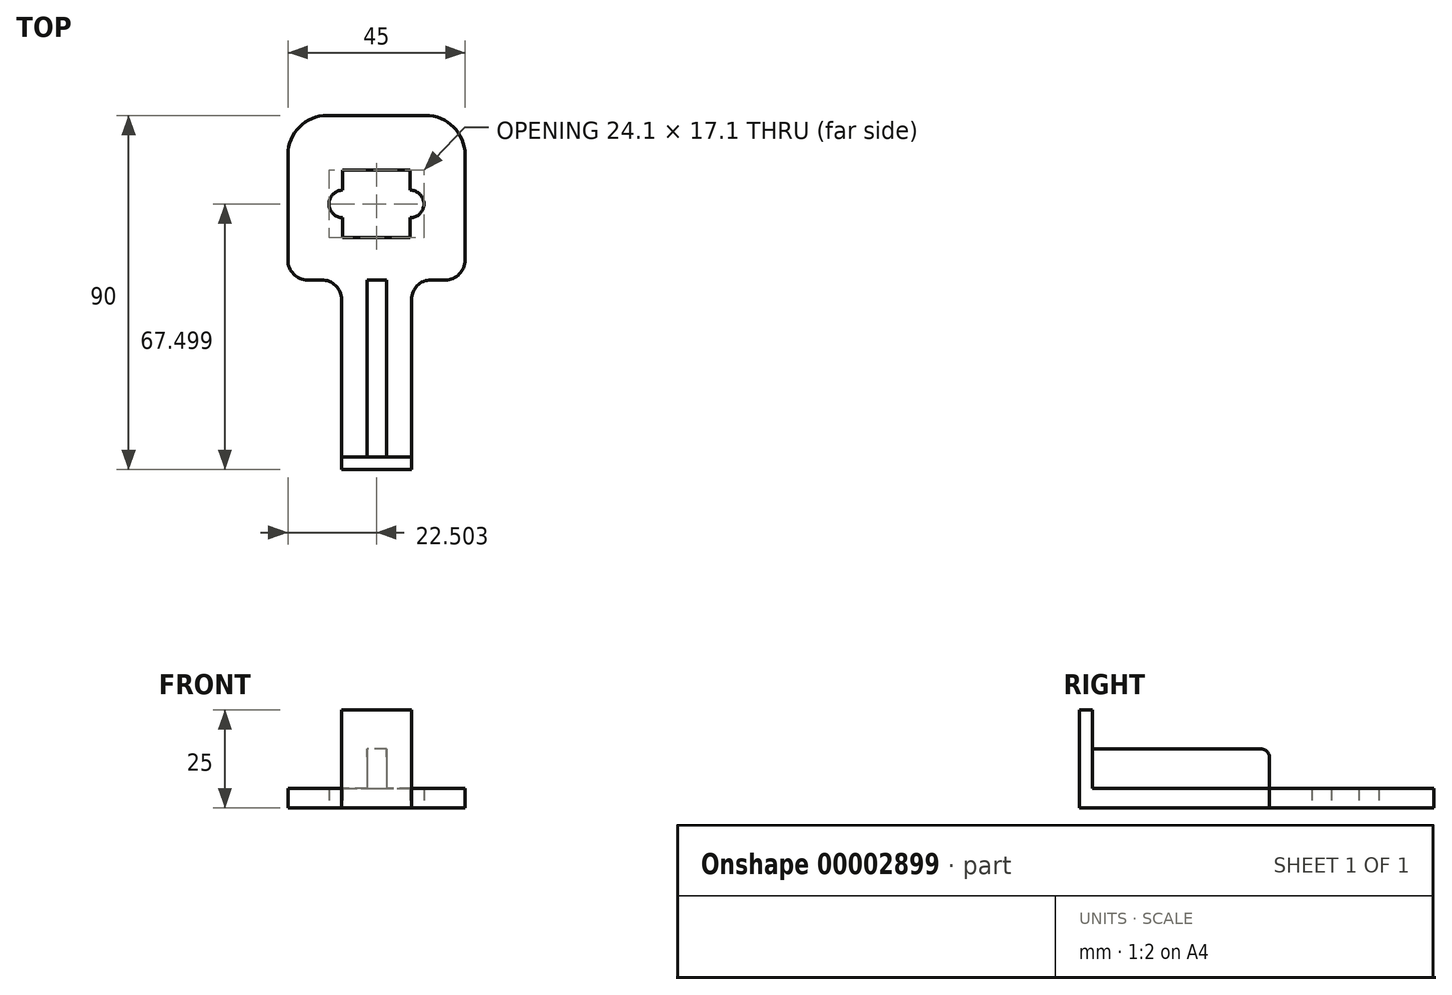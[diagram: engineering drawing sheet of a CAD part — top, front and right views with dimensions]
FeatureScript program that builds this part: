
annotation { "Feature Type Name" : "Feature", "Feature Type Description" : "" }
export const myFeature = defineFeature(function(context is Context, id is Id, definition is map)
    precondition{}
    {
        {
            var Q0;
            Q0=qCreatedBy(makeId("Top.planeOp"),FACE);
            var sketch = newSketch(context, id + "F0", { "sketchPlane" : qUnion([Q0])});
            skLineSegment(sketch, "E0.bottom", {"start": v(-64.63, 13.52) * mm, "end": v(-47.53, 13.52) * mm});
            skLineSegment(sketch, "E0.top", {"start": v(-64.63, -3.58) * mm, "end": v(-47.53, -3.58) * mm});
            skLineSegment(sketch, "E0.left", {"start": v(-64.63, 13.52) * mm, "end": v(-64.63, 8.47) * mm});
            skLineSegment(sketch, "E0.right", {"start": v(-47.53, 13.52) * mm, "end": v(-47.53, 8.47) * mm});
            skArc(sketch, "E1", {"start": v(-64.63, 8.47) * mm, "mid": v(-68.13, 4.97) * mm, "end": v(-64.63, 1.47) * mm});
            skArc(sketch, "E2", {"start": v(-47.53, 1.47) * mm, "mid": v(-44.03, 4.97) * mm, "end": v(-47.53, 8.47) * mm});
            skLineSegment(sketch, "E3.trimOffspring", {"start": v(-64.63, 1.47) * mm, "end": v(-64.63, -3.58) * mm});
            skLineSegment(sketch, "E4.trimOffspring", {"start": v(-47.53, 1.47) * mm, "end": v(-47.53, -3.58) * mm});
            skLineSegment(sketch, "E5.bottom", {"start": v(-68.58, 27.47) * mm, "end": v(-43.58, 27.47) * mm});
            skLineSegment(sketch, "E5.top", {"start": v(-64.97, -62.53) * mm, "end": v(-47.18, -62.53) * mm});
            skLineSegment(sketch, "E5.left", {"start": v(-78.58, 17.47) * mm, "end": v(-78.58, -9.33) * mm});
            skLineSegment(sketch, "E5.right", {"start": v(-33.58, 17.47) * mm, "end": v(-33.58, -9.33) * mm});
            skPoint(sketch, "E6.visualSharp", {"position": v(-78.58, 27.47) * mm});
            skArc(sketch, "E6.filletArc", {"start": v(-68.58, 27.47) * mm, "mid": v(-75.65, 24.54) * mm, "end": v(-78.58, 17.47) * mm});
            skPoint(sketch, "E7.visualSharp", {"position": v(-33.58, 27.47) * mm});
            skArc(sketch, "E7.filletArc", {"start": v(-33.58, 17.47) * mm, "mid": v(-36.5, 24.54) * mm, "end": v(-43.58, 27.47) * mm});
            skLineSegment(sketch, "E8.bottom", {"start": v(-73.58, -14.33) * mm, "end": v(-69.97, -14.33) * mm});
            skLineSegment(sketch, "E8.right", {"start": v(-64.97, -19.33) * mm, "end": v(-64.97, -62.53) * mm});
            skLineSegment(sketch, "E9.0.MirrorCS", {"start": v(-38.58, -14.33) * mm, "end": v(-42.18, -14.33) * mm});
            skLineSegment(sketch, "E9.1.MirrorCS", {"start": v(-47.18, -19.33) * mm, "end": v(-47.18, -62.53) * mm});
            skPoint(sketch, "E10.orphan", {"position": v(-33.58, -62.53) * mm});
            skPoint(sketch, "E11.visualSharp", {"position": v(-78.58, -14.33) * mm});
            skArc(sketch, "E11.filletArc", {"start": v(-78.58, -9.33) * mm, "mid": v(-77.11, -12.86) * mm, "end": v(-73.58, -14.33) * mm});
            skPoint(sketch, "E12.visualSharp", {"position": v(-64.97, -14.33) * mm});
            skArc(sketch, "E12.filletArc", {"start": v(-64.97, -19.33) * mm, "mid": v(-66.43, -15.8) * mm, "end": v(-69.97, -14.33) * mm});
            skPoint(sketch, "E13.visualSharp", {"position": v(-47.18, -14.33) * mm});
            skArc(sketch, "E13.filletArc", {"start": v(-42.18, -14.33) * mm, "mid": v(-45.72, -15.8) * mm, "end": v(-47.18, -19.33) * mm});
            skPoint(sketch, "E14.visualSharp", {"position": v(-33.58, -14.33) * mm});
            skArc(sketch, "E14.filletArc", {"start": v(-38.58, -14.33) * mm, "mid": v(-35.04, -12.86) * mm, "end": v(-33.58, -9.33) * mm});
            skLineSegment(sketch, "E15", {"start": v(-64.97, -59.3) * mm, "end": v(-47.18, -59.3) * mm});
            skSolve(sketch);
        }
        {
            var Q0;
            Q0 = qSketchRegion(id + "F0", true);
            extrude(context, id + "F1", {"entities" : qUnion([Q0]), "depth" : 5 * mm});
        }
        {
            var Q0;
            {var subQ2=sQuery(id+"F0.wireOp",EDGE,"E5.top");Q0=makeQuery(id+"F0.imprint","IMPRINT",FACE,{"disambiguationData":[TD([[makeQuery(id+"F0.imprint","IMPRINT",EDGE,{"derivedFrom":subQ2}),1.0]])]});}
            extrude(context, id + "F2", {"entities" : qUnion([Q0]), "operationType" : NewBodyOperationType.ADD, "depth" : 25 * mm});
        }
        {
            var Q0;
            Q0=makeQuery(id+"F1.opExtrude","CAP_FACE",FACE,{"disambiguationData":[OSD([sQuery(id+"F0.wireOp",EDGE,"E0.bottom"),sQuery(id+"F0.wireOp",EDGE,"E0.top"),sQuery(id+"F0.wireOp",EDGE,"E0.left"),sQuery(id+"F0.wireOp",EDGE,"E0.right"),sQuery(id+"F0.wireOp",EDGE,"E1"),sQuery(id+"F0.wireOp",EDGE,"E2"),sQuery(id+"F0.wireOp",EDGE,"E3.trimOffspring"),sQuery(id+"F0.wireOp",EDGE,"E4.trimOffspring"),sQuery(id+"F0.wireOp",EDGE,"E5.bottom"),sQuery(id+"F0.wireOp",EDGE,"E5.top"),sQuery(id+"F0.wireOp",EDGE,"E5.left"),sQuery(id+"F0.wireOp",EDGE,"E5.right"),sQuery(id+"F0.wireOp",EDGE,"E6.filletArc"),sQuery(id+"F0.wireOp",EDGE,"E7.filletArc"),sQuery(id+"F0.wireOp",EDGE,"E8.bottom"),sQuery(id+"F0.wireOp",EDGE,"E8.right"),sQuery(id+"F0.wireOp",EDGE,"E9.0.MirrorCS"),sQuery(id+"F0.wireOp",EDGE,"E9.1.MirrorCS"),sQuery(id+"F0.wireOp",EDGE,"E11.filletArc"),sQuery(id+"F0.wireOp",EDGE,"E12.filletArc"),sQuery(id+"F0.wireOp",EDGE,"E13.filletArc"),sQuery(id+"F0.wireOp",EDGE,"E14.filletArc")])],"isStart":false});
            var sketch = newSketch(context, id + "F3", { "sketchPlane" : qUnion([Q0])});
            skLineSegment(sketch, "E16.bottom", {"start": v(-58.46, -14.33) * mm, "end": v(-53.5, -14.33) * mm});
            skLineSegment(sketch, "E16.top", {"start": v(-58.46, -59.3) * mm, "end": v(-53.5, -59.3) * mm});
            skLineSegment(sketch, "E16.left", {"start": v(-58.46, -14.33) * mm, "end": v(-58.46, -59.3) * mm});
            skLineSegment(sketch, "E16.right", {"start": v(-53.5, -14.33) * mm, "end": v(-53.5, -59.3) * mm});
            skSolve(sketch);
        }
        {
            var Q0;
            Q0=makeQuery(id+"F3.imprint","IMPRINT",FACE,{"disambiguationData":[TD([[makeQuery(id+"F3.imprint","IMPRINT",EDGE,{"derivedFrom":sQuery(id+"F3.wireOp",EDGE,"E16.bottom")}),-1.0]])]});
            extrude(context, id + "F4", {"entities" : qUnion([Q0]), "operationType" : NewBodyOperationType.ADD, "depth" : 10 * mm});
        }
        {
            var Q0;
            Q0=makeQuery(id+"F4.opExtrude","CAP_EDGE",EDGE,{"disambiguationData":[OSD([sQuery(id+"F3.wireOp",EDGE,"E16.right")])],"isStart":true});
            var Q1;
            Q1=makeQuery(id+"F4.opExtrude","SWEPT_EDGE",EDGE,{"disambiguationData":[OSD([sQuery(id+"F0.wireOp",EDGE,"E0.bottom"),sQuery(id+"F0.wireOp",EDGE,"E0.top"),sQuery(id+"F0.wireOp",EDGE,"E0.left"),sQuery(id+"F0.wireOp",EDGE,"E0.right"),sQuery(id+"F0.wireOp",EDGE,"E1"),sQuery(id+"F0.wireOp",EDGE,"E2"),sQuery(id+"F0.wireOp",EDGE,"E3.trimOffspring"),sQuery(id+"F0.wireOp",EDGE,"E4.trimOffspring"),sQuery(id+"F0.wireOp",EDGE,"E5.bottom"),sQuery(id+"F0.wireOp",EDGE,"E5.top"),sQuery(id+"F0.wireOp",EDGE,"E5.left"),sQuery(id+"F0.wireOp",EDGE,"E5.right"),sQuery(id+"F0.wireOp",EDGE,"E6.filletArc"),sQuery(id+"F0.wireOp",EDGE,"E7.filletArc"),sQuery(id+"F0.wireOp",EDGE,"E8.bottom"),sQuery(id+"F0.wireOp",EDGE,"E8.right"),sQuery(id+"F0.wireOp",EDGE,"E9.0.MirrorCS"),sQuery(id+"F0.wireOp",EDGE,"E9.1.MirrorCS"),sQuery(id+"F0.wireOp",EDGE,"E11.filletArc"),sQuery(id+"F0.wireOp",EDGE,"E12.filletArc"),sQuery(id+"F0.wireOp",EDGE,"E13.filletArc"),sQuery(id+"F0.wireOp",EDGE,"E14.filletArc"),sQuery(id+"F0.wireOp",EDGE,"E15"),sQuery(id+"F3.wireOp",EDGE,"E16.top"),sQuery(id+"F3.wireOp",EDGE,"E16.right")])]});
            var Q2;
            Q2=makeQuery(id+"F4.opExtrude","CAP_EDGE",EDGE,{"disambiguationData":[OSD([sQuery(id+"F3.wireOp",EDGE,"E16.top")])],"isStart":false});
            var Q3;
            Q3=makeQuery(id+"F4.opExtrude","SWEPT_EDGE",EDGE,{"disambiguationData":[OSD([sQuery(id+"F0.wireOp",EDGE,"E0.bottom"),sQuery(id+"F0.wireOp",EDGE,"E0.top"),sQuery(id+"F0.wireOp",EDGE,"E0.left"),sQuery(id+"F0.wireOp",EDGE,"E0.right"),sQuery(id+"F0.wireOp",EDGE,"E1"),sQuery(id+"F0.wireOp",EDGE,"E2"),sQuery(id+"F0.wireOp",EDGE,"E3.trimOffspring"),sQuery(id+"F0.wireOp",EDGE,"E4.trimOffspring"),sQuery(id+"F0.wireOp",EDGE,"E5.bottom"),sQuery(id+"F0.wireOp",EDGE,"E5.top"),sQuery(id+"F0.wireOp",EDGE,"E5.left"),sQuery(id+"F0.wireOp",EDGE,"E5.right"),sQuery(id+"F0.wireOp",EDGE,"E6.filletArc"),sQuery(id+"F0.wireOp",EDGE,"E7.filletArc"),sQuery(id+"F0.wireOp",EDGE,"E8.bottom"),sQuery(id+"F0.wireOp",EDGE,"E8.right"),sQuery(id+"F0.wireOp",EDGE,"E9.0.MirrorCS"),sQuery(id+"F0.wireOp",EDGE,"E9.1.MirrorCS"),sQuery(id+"F0.wireOp",EDGE,"E11.filletArc"),sQuery(id+"F0.wireOp",EDGE,"E12.filletArc"),sQuery(id+"F0.wireOp",EDGE,"E13.filletArc"),sQuery(id+"F0.wireOp",EDGE,"E14.filletArc"),sQuery(id+"F0.wireOp",EDGE,"E15"),sQuery(id+"F3.wireOp",EDGE,"E16.top"),sQuery(id+"F3.wireOp",EDGE,"E16.left")])]});
            var Q4;
            Q4=makeQuery(id+"F4.opExtrude","CAP_EDGE",EDGE,{"disambiguationData":[OSD([sQuery(id+"F3.wireOp",EDGE,"E16.left")])],"isStart":true});
            var Q5;
            Q5=makeQuery(id+"F4.opExtrude","CAP_EDGE",EDGE,{"disambiguationData":[OSD([sQuery(id+"F3.wireOp",EDGE,"E16.bottom")])],"isStart":false});
            var Q6;
            Q6=makeQuery(id+"F4.opExtrude","CAP_EDGE",EDGE,{"disambiguationData":[OSD([sQuery(id+"F3.wireOp",EDGE,"E16.bottom")])],"isStart":true});
            fillet(context, id + "F5", {"entities" : qUnion([Q0, Q1, Q2, Q3, Q4, Q5, Q6]), "radius" : 2 * mm, "tangentPropagation" : true, "allowEdgeOverflow" : false});
        }
    });
